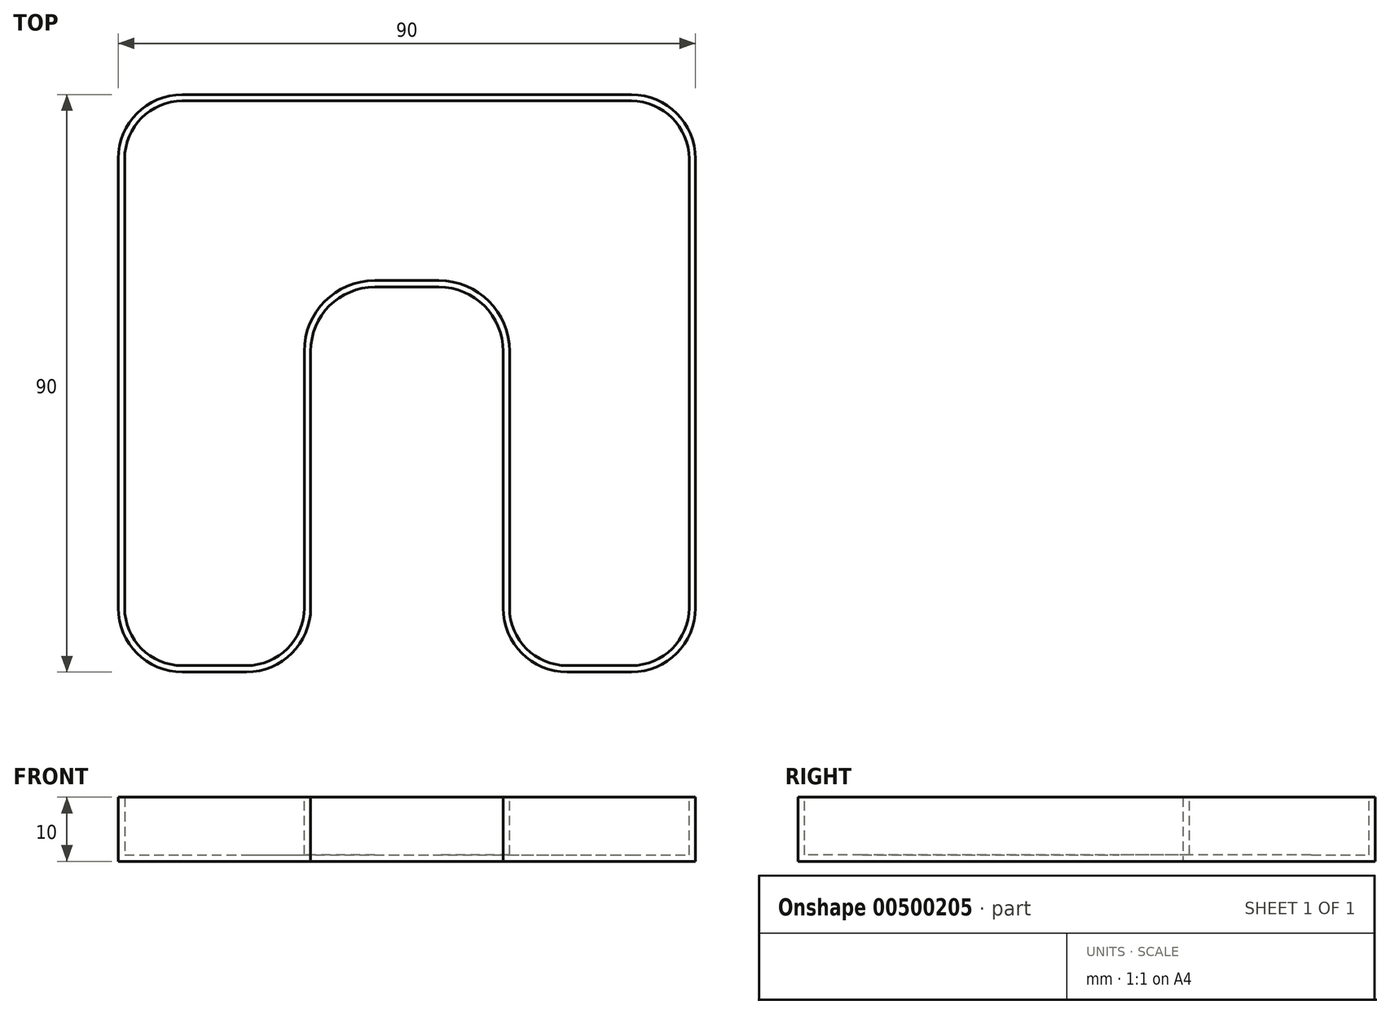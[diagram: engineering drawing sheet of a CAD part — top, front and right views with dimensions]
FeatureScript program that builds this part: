
annotation { "Feature Type Name" : "Feature", "Feature Type Description" : "" }
export const myFeature = defineFeature(function(context is Context, id is Id, definition is map)
    precondition{}
    {
        {
            var Q0;
            Q0=qCreatedBy(makeId("Top.planeOp"),FACE);
            var sketch = newSketch(context, id + "F0", { "sketchPlane" : qUnion([Q0])});
            skLineSegment(sketch, "E0.bottom", {"start": v(-54.72, 50.54) * mm, "end": v(35.28, 50.54) * mm});
            skLineSegment(sketch, "E0.top", {"start": v(-54.72, -39.46) * mm, "end": v(-24.72, -39.46) * mm});
            skLineSegment(sketch, "E0.left", {"start": v(-54.72, 50.54) * mm, "end": v(-54.72, -39.46) * mm});
            skLineSegment(sketch, "E0.right", {"start": v(35.28, 50.54) * mm, "end": v(35.28, -39.46) * mm});
            skLineSegment(sketch, "E1", {"start": v(-24.72, -39.46) * mm, "end": v(-24.72, 20.54) * mm});
            skLineSegment(sketch, "E2", {"start": v(-24.72, 20.54) * mm, "end": v(5.28, 20.54) * mm});
            skLineSegment(sketch, "E3", {"start": v(5.28, 20.54) * mm, "end": v(5.28, -39.46) * mm});
            skLineSegment(sketch, "E4.trimOffspring", {"start": v(5.28, -39.46) * mm, "end": v(35.28, -39.46) * mm});
            skSolve(sketch);
        }
        {
            var Q0;
            Q0 = qSketchRegion(id + "F0", true);
            extrude(context, id + "F1", {"entities" : qUnion([Q0]), "depth" : 10 * mm});
        }
        {
            var Q0;
            Q0=makeQuery(id+"F1.opExtrude","SWEPT_EDGE",EDGE,{"disambiguationData":[OSD([sQuery(id+"F0.wireOp",EDGE,"E0.bottom"),sQuery(id+"F0.wireOp",EDGE,"E0.right")])]});
            var Q1;
            Q1=makeQuery(id+"F1.opExtrude","SWEPT_EDGE",EDGE,{"disambiguationData":[OSD([sQuery(id+"F0.wireOp",EDGE,"E0.right"),sQuery(id+"F0.wireOp",EDGE,"E4.trimOffspring")])]});
            var Q2;
            Q2=makeQuery(id+"F1.opExtrude","SWEPT_EDGE",EDGE,{"disambiguationData":[OSD([sQuery(id+"F0.wireOp",EDGE,"E1"),sQuery(id+"F0.wireOp",EDGE,"E2")])]});
            var Q3;
            Q3=makeQuery(id+"F1.opExtrude","SWEPT_EDGE",EDGE,{"disambiguationData":[OSD([sQuery(id+"F0.wireOp",EDGE,"E0.top"),sQuery(id+"F0.wireOp",EDGE,"E1")])]});
            var Q4;
            Q4=makeQuery(id+"F1.opExtrude","SWEPT_EDGE",EDGE,{"disambiguationData":[OSD([sQuery(id+"F0.wireOp",EDGE,"E0.top"),sQuery(id+"F0.wireOp",EDGE,"E0.left")])]});
            var Q5;
            Q5=makeQuery(id+"F1.opExtrude","SWEPT_EDGE",EDGE,{"disambiguationData":[OSD([sQuery(id+"F0.wireOp",EDGE,"E3"),sQuery(id+"F0.wireOp",EDGE,"E4.trimOffspring")])]});
            var Q6;
            Q6=makeQuery(id+"F1.opExtrude","SWEPT_EDGE",EDGE,{"disambiguationData":[OSD([sQuery(id+"F0.wireOp",EDGE,"E2"),sQuery(id+"F0.wireOp",EDGE,"E3")])]});
            var Q7;
            Q7=makeQuery(id+"F1.opExtrude","SWEPT_EDGE",EDGE,{"disambiguationData":[OSD([sQuery(id+"F0.wireOp",EDGE,"E0.bottom"),sQuery(id+"F0.wireOp",EDGE,"E0.left")])]});
            fillet(context, id + "F2", {"entities" : qUnion([Q0, Q1, Q2, Q3, Q4, Q5, Q6, Q7]), "radius" : 10 * mm, "tangentPropagation" : true, "allowEdgeOverflow" : false});
        }
        {
            var Q0;
            Q0=makeQuery(id+"F1.opExtrude","CAP_FACE",FACE,{"disambiguationData":[OSD([sQuery(id+"F0.wireOp",EDGE,"E0.bottom"),sQuery(id+"F0.wireOp",EDGE,"E0.top"),sQuery(id+"F0.wireOp",EDGE,"E0.left"),sQuery(id+"F0.wireOp",EDGE,"E0.right"),sQuery(id+"F0.wireOp",EDGE,"E1"),sQuery(id+"F0.wireOp",EDGE,"E2"),sQuery(id+"F0.wireOp",EDGE,"E3"),sQuery(id+"F0.wireOp",EDGE,"E4.trimOffspring")])],"isStart":false});
            shell(context, id + "F3", {"entities" : qUnion([Q0]), "thickness" : 1 * mm});
        }
    });
